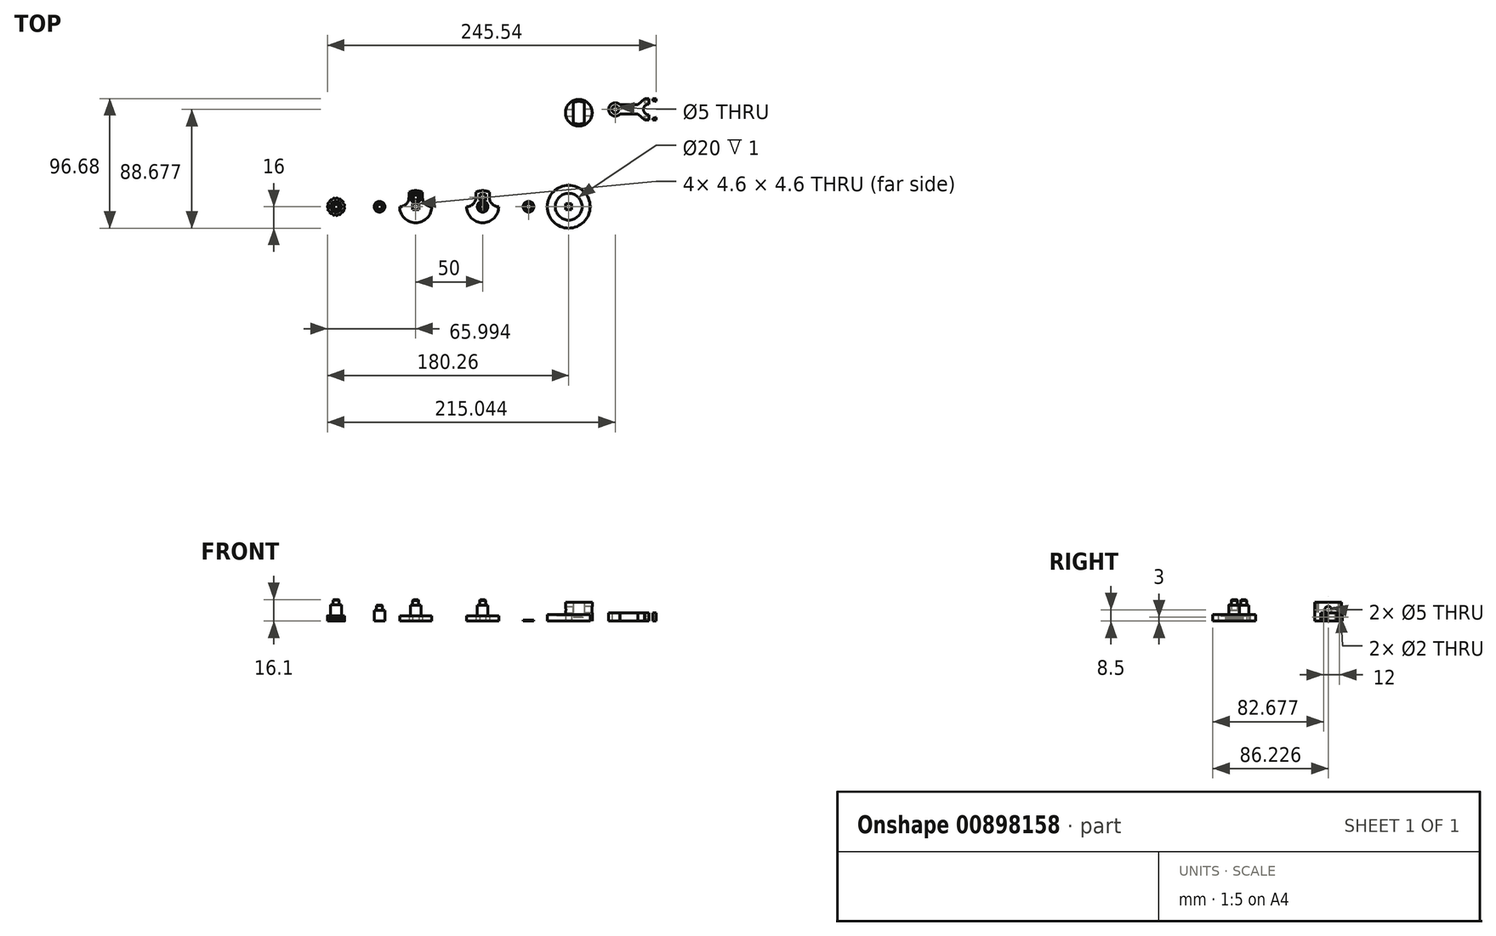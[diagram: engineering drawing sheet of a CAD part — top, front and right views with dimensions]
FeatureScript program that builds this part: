
annotation { "Feature Type Name" : "Feature", "Feature Type Description" : "" }
export const myFeature = defineFeature(function(context is Context, id is Id, definition is map)
    precondition{}
    {
        {
            var Q0;
            Q0=qCreatedBy(makeId("Top.planeOp"),FACE);
            var sketch = newSketch(context, id + "F0", { "sketchPlane" : qUnion([Q0])});
            skLineSegment(sketch, "E0", {"start": v(0, 27.68) * mm, "end": v(0, 49.61) * mm});
            skCircle(sketch, "E1", {"center": v(14.78, 62.68) * mm, "radius": 2.5 * mm});
            skPoint(sketch, "E2", {"position": v(39.78, 62.68) * mm});
            skArc(sketch, "E3", {"start": v(39.78, 58.68) * mm, "mid": v(35.78, 62.68) * mm, "end": v(39.78, 66.68) * mm});
            skLineSegment(sketch, "E4", {"start": v(39.78, 66.68) * mm, "end": v(39.78, 70.68) * mm});
            skLineSegment(sketch, "E5", {"start": v(39.78, 58.68) * mm, "end": v(39.78, 54.68) * mm});
            skPoint(sketch, "E6", {"position": v(42.78, 62.68) * mm});
            skArc(sketch, "E7", {"start": v(42.78, 66.68) * mm, "mid": v(46.78, 62.68) * mm, "end": v(42.78, 58.68) * mm});
            skArc(sketch, "E8", {"start": v(42.78, 69.18) * mm, "mid": v(49.28, 62.68) * mm, "end": v(42.78, 56.18) * mm});
            skLineSegment(sketch, "E9", {"start": v(42.78, 66.68) * mm, "end": v(42.78, 69.18) * mm});
            skLineSegment(sketch, "E10", {"start": v(42.78, 69.18) * mm, "end": v(42.78, 70.68) * mm});
            skLineSegment(sketch, "E11", {"start": v(42.78, 70.68) * mm, "end": v(45.28, 70.68) * mm});
            skLineSegment(sketch, "E12", {"start": v(45.28, 70.68) * mm, "end": v(45.28, 68.68) * mm});
            skLineSegment(sketch, "E13", {"start": v(42.78, 58.68) * mm, "end": v(42.78, 56.18) * mm});
            skLineSegment(sketch, "E14", {"start": v(42.78, 56.18) * mm, "end": v(42.78, 54.68) * mm});
            skLineSegment(sketch, "E15", {"start": v(42.78, 54.68) * mm, "end": v(45.28, 54.68) * mm});
            skLineSegment(sketch, "E16", {"start": v(45.28, 54.68) * mm, "end": v(45.28, 56.68) * mm});
            skCircle(sketch, "E17", {"center": v(-12.45, 60.23) * mm, "radius": 10 * mm});
            skLineSegment(sketch, "E18", {"start": v(18.36, 66.18) * mm, "end": v(31.78, 66.18) * mm});
            skLineSegment(sketch, "E19", {"start": v(39.78, 70.68) * mm, "end": v(36.78, 70.68) * mm});
            skLineSegment(sketch, "E20", {"start": v(36.78, 70.68) * mm, "end": v(31.78, 66.18) * mm});
            skLineSegment(sketch, "E21", {"start": v(39.78, 62.68) * mm, "end": v(42.78, 62.68) * mm});
            skLineSegment(sketch, "E22.MirrorCS", {"start": v(18.36, 59.18) * mm, "end": v(31.78, 59.18) * mm});
            skLineSegment(sketch, "E23.MirrorCS", {"start": v(39.78, 54.68) * mm, "end": v(36.78, 54.68) * mm});
            skLineSegment(sketch, "E24.MirrorCS", {"start": v(36.78, 54.68) * mm, "end": v(31.78, 59.18) * mm});
            skArc(sketch, "E25", {"start": v(18.36, 66.18) * mm, "mid": v(9.78, 62.68) * mm, "end": v(18.36, 59.18) * mm});
            skCircle(sketch, "E26", {"center": v(-134.27, -10) * mm, "radius": 12 * mm});
            skCircle(sketch, "E27", {"center": v(-134.27, -3) * mm, "radius": 4 * mm});
            skLineSegment(sketch, "E28.bottom", {"start": v(-131.97, -7.7) * mm, "end": v(-136.57, -7.7) * mm});
            skLineSegment(sketch, "E28.top", {"start": v(-131.97, -12.3) * mm, "end": v(-136.57, -12.3) * mm});
            skLineSegment(sketch, "E28.left", {"start": v(-131.97, -7.7) * mm, "end": v(-131.97, -12.3) * mm});
            skLineSegment(sketch, "E28.right", {"start": v(-136.57, -7.7) * mm, "end": v(-136.57, -12.3) * mm});
            skLineSegment(sketch, "E29.bottom", {"start": v(-132.02, -0.75) * mm, "end": v(-136.52, -0.75) * mm});
            skLineSegment(sketch, "E29.top", {"start": v(-132.02, -5.25) * mm, "end": v(-136.52, -5.25) * mm});
            skLineSegment(sketch, "E29.left", {"start": v(-132.02, -0.75) * mm, "end": v(-132.02, -5.25) * mm});
            skLineSegment(sketch, "E29.right", {"start": v(-136.52, -0.75) * mm, "end": v(-136.52, -5.25) * mm});
            skCircle(sketch, "E30", {"center": v(-84.27, -10) * mm, "radius": 12 * mm});
            skPoint(sketch, "E30.centerSnap0", {"position": v(-131.97, -10) * mm});
            skPoint(sketch, "E31", {"position": v(-84.27, -3) * mm});
            skPoint(sketch, "E31.positionSnap0", {"position": v(-132.02, -3) * mm});
            skLineSegment(sketch, "E32.bottom", {"start": v(-81.97, -0.7) * mm, "end": v(-86.57, -0.7) * mm});
            skLineSegment(sketch, "E32.top", {"start": v(-81.97, -5.3) * mm, "end": v(-86.57, -5.3) * mm});
            skLineSegment(sketch, "E32.left", {"start": v(-81.97, -0.7) * mm, "end": v(-81.97, -5.3) * mm});
            skLineSegment(sketch, "E32.right", {"start": v(-86.57, -0.7) * mm, "end": v(-86.57, -5.3) * mm});
            skCircle(sketch, "E33", {"center": v(-84.27, -10) * mm, "radius": 4 * mm});
            skCircle(sketch, "E34", {"center": v(-161.27, -10) * mm, "radius": 4 * mm});
            skLineSegment(sketch, "E35.bottom", {"start": v(-159.02, -7.75) * mm, "end": v(-163.52, -7.75) * mm});
            skLineSegment(sketch, "E35.top", {"start": v(-159.02, -12.25) * mm, "end": v(-163.52, -12.25) * mm});
            skLineSegment(sketch, "E35.left", {"start": v(-159.02, -7.75) * mm, "end": v(-159.02, -12.25) * mm});
            skLineSegment(sketch, "E35.right", {"start": v(-163.52, -7.75) * mm, "end": v(-163.52, -12.25) * mm});
            skLineSegment(sketch, "E36", {"start": v(-122.27, -10) * mm, "end": v(-122.27, -3.2) * mm});
            skPoint(sketch, "E37.startSnap0", {"position": v(-134.27, -5.25) * mm});
            skPoint(sketch, "E38", {"position": v(-122.27, -3) * mm});
            skArc(sketch, "E39", {"start": v(-122.27, -10) * mm, "mid": v(-127.22, -7.95) * mm, "end": v(-129.27, -3) * mm});
            skLineSegment(sketch, "E40", {"start": v(-129.27, -3) * mm, "end": v(-129.27, 0.9) * mm});
            skLineSegment(sketch, "E41", {"start": v(-134.27, -33.2) * mm, "end": v(-134.27, -38.63) * mm});
            skPoint(sketch, "E41.startSnap0", {"position": v(-134.27, -12.3) * mm});
            skArc(sketch, "E42.MirrorCS", {"start": v(-146.27, -10) * mm, "mid": v(-141.32, -7.95) * mm, "end": v(-139.27, -3) * mm});
            skLineSegment(sketch, "E43.MirrorCS", {"start": v(-139.27, -3) * mm, "end": v(-139.27, 0.9) * mm});
            skLineSegment(sketch, "E44.1.0.0", {"start": v(-79.27, -3) * mm, "end": v(-79.27, 0.9) * mm});
            skArc(sketch, "E44.1.0.1", {"start": v(-72.27, -10) * mm, "mid": v(-77.22, -7.95) * mm, "end": v(-79.27, -3) * mm});
            skArc(sketch, "E44.1.0.2", {"start": v(-96.27, -10) * mm, "mid": v(-91.32, -7.95) * mm, "end": v(-89.27, -3) * mm});
            skLineSegment(sketch, "E44.1.0.3", {"start": v(-89.27, -3) * mm, "end": v(-89.27, 0.9) * mm});
            skLineSegment(sketch, "E44.direction1", {"start": v(-146.27, -10) * mm, "end": v(-96.27, -10) * mm, "construction": true});
            skLineSegment(sketch, "E45.bottom", {"start": v(-82.02, -7.75) * mm, "end": v(-86.52, -7.75) * mm});
            skLineSegment(sketch, "E45.top", {"start": v(-82.02, -12.25) * mm, "end": v(-86.52, -12.25) * mm});
            skLineSegment(sketch, "E45.left", {"start": v(-82.02, -7.75) * mm, "end": v(-82.02, -12.25) * mm});
            skLineSegment(sketch, "E45.right", {"start": v(-86.52, -7.75) * mm, "end": v(-86.52, -12.25) * mm});
            skCircle(sketch, "E46", {"center": v(-20, -10) * mm, "radius": 16 * mm});
            skLineSegment(sketch, "E47.bottom", {"start": v(-17.7, -7.7) * mm, "end": v(-22.3, -7.7) * mm});
            skLineSegment(sketch, "E47.top", {"start": v(-17.7, -12.3) * mm, "end": v(-22.3, -12.3) * mm});
            skLineSegment(sketch, "E47.left", {"start": v(-17.7, -7.7) * mm, "end": v(-17.7, -12.3) * mm});
            skLineSegment(sketch, "E47.right", {"start": v(-22.3, -7.7) * mm, "end": v(-22.3, -12.3) * mm});
            skCircle(sketch, "E48", {"center": v(-50, -10) * mm, "radius": 4 * mm});
            skLineSegment(sketch, "E49.bottom", {"start": v(-47.7, -7.7) * mm, "end": v(-52.3, -7.7) * mm});
            skLineSegment(sketch, "E49.top", {"start": v(-47.7, -12.3) * mm, "end": v(-52.3, -12.3) * mm});
            skLineSegment(sketch, "E49.left", {"start": v(-47.7, -7.7) * mm, "end": v(-47.7, -12.3) * mm});
            skLineSegment(sketch, "E49.right", {"start": v(-52.3, -7.7) * mm, "end": v(-52.3, -12.3) * mm});
            skCircle(sketch, "E50", {"center": v(-193.76, -10) * mm, "radius": 4 * mm});
            skCircle(sketch, "E51", {"center": v(-193.76, -10) * mm, "radius": 6 * mm});
            skLineSegment(sketch, "E52.bottom", {"start": v(-191.51, -7.75) * mm, "end": v(-196.01, -7.75) * mm});
            skLineSegment(sketch, "E52.top", {"start": v(-191.51, -12.25) * mm, "end": v(-196.01, -12.25) * mm});
            skLineSegment(sketch, "E52.left", {"start": v(-191.51, -7.75) * mm, "end": v(-191.51, -12.25) * mm});
            skLineSegment(sketch, "E52.right", {"start": v(-196.01, -7.75) * mm, "end": v(-196.01, -12.25) * mm});
            skCircle(sketch, "E53", {"center": v(-193.76, -10) * mm, "radius": 6.5 * mm});
            skLineSegment(sketch, "E54", {"start": v(-193.76, -4) * mm, "end": v(-193.76, -3.5) * mm});
            skLineSegment(sketch, "E55.1.0", {"start": v(-195.01, -4.13) * mm, "end": v(-195.11, -3.64) * mm});
            skLineSegment(sketch, "E55.2.0", {"start": v(-196.2, -4.52) * mm, "end": v(-196.4, -4.06) * mm});
            skLineSegment(sketch, "E55.3.0", {"start": v(-197.29, -5.15) * mm, "end": v(-197.58, -4.74) * mm});
            skLineSegment(sketch, "E55.4.0", {"start": v(-198.22, -5.99) * mm, "end": v(-198.6, -5.65) * mm});
            skLineSegment(sketch, "E55.5.0", {"start": v(-198.96, -7) * mm, "end": v(-199.4, -6.75) * mm});
            skLineSegment(sketch, "E55.6.0", {"start": v(-199.47, -8.15) * mm, "end": v(-199.94, -8) * mm});
            skLineSegment(sketch, "E55.7.0", {"start": v(-199.73, -9.37) * mm, "end": v(-200.23, -9.32) * mm});
            skLineSegment(sketch, "E55.8.0", {"start": v(-199.73, -10.63) * mm, "end": v(-200.23, -10.68) * mm});
            skLineSegment(sketch, "E55.9.0", {"start": v(-199.47, -11.85) * mm, "end": v(-199.94, -12) * mm});
            skLineSegment(sketch, "E55.10.0", {"start": v(-198.96, -13) * mm, "end": v(-199.4, -13.25) * mm});
            skLineSegment(sketch, "E55.11.0", {"start": v(-198.22, -14.01) * mm, "end": v(-198.6, -14.35) * mm});
            skLineSegment(sketch, "E55.12.0", {"start": v(-197.29, -14.85) * mm, "end": v(-197.58, -15.26) * mm});
            skLineSegment(sketch, "E55.13.0", {"start": v(-196.2, -15.48) * mm, "end": v(-196.4, -15.94) * mm});
            skLineSegment(sketch, "E55.14.0", {"start": v(-195.01, -15.87) * mm, "end": v(-195.11, -16.36) * mm});
            skLineSegment(sketch, "E55.15.0", {"start": v(-193.76, -16) * mm, "end": v(-193.76, -16.5) * mm});
            skLineSegment(sketch, "E55.16.0", {"start": v(-192.52, -15.87) * mm, "end": v(-192.41, -16.36) * mm});
            skLineSegment(sketch, "E55.17.0", {"start": v(-191.32, -15.48) * mm, "end": v(-191.12, -15.94) * mm});
            skLineSegment(sketch, "E55.18.0", {"start": v(-190.24, -14.85) * mm, "end": v(-189.94, -15.26) * mm});
            skLineSegment(sketch, "E55.19.0", {"start": v(-189.3, -14.01) * mm, "end": v(-188.93, -14.35) * mm});
            skLineSegment(sketch, "E55.20.0", {"start": v(-188.57, -13) * mm, "end": v(-188.13, -13.25) * mm});
            skLineSegment(sketch, "E55.21.0", {"start": v(-188.06, -11.85) * mm, "end": v(-187.58, -12) * mm});
            skLineSegment(sketch, "E55.22.0", {"start": v(-187.8, -10.63) * mm, "end": v(-187.3, -10.68) * mm});
            skLineSegment(sketch, "E55.23.0", {"start": v(-187.8, -9.37) * mm, "end": v(-187.3, -9.32) * mm});
            skLineSegment(sketch, "E55.24.0", {"start": v(-188.06, -8.15) * mm, "end": v(-187.58, -8) * mm});
            skLineSegment(sketch, "E55.25.0", {"start": v(-188.57, -7) * mm, "end": v(-188.13, -6.75) * mm});
            skLineSegment(sketch, "E55.26.0", {"start": v(-189.3, -5.99) * mm, "end": v(-188.93, -5.65) * mm});
            skLineSegment(sketch, "E55.27.0", {"start": v(-190.24, -5.15) * mm, "end": v(-189.94, -4.74) * mm});
            skLineSegment(sketch, "E55.28.0", {"start": v(-191.32, -4.52) * mm, "end": v(-191.12, -4.06) * mm});
            skLineSegment(sketch, "E55.29.0", {"start": v(-192.52, -4.13) * mm, "end": v(-192.41, -3.64) * mm});
            skSolve(sketch);
        }
        {
            var Q0;
            Q0=makeQuery(id+"F0.imprint","IMPRINT",FACE,{"disambiguationData":[TD([[makeQuery(id+"F0.imprint","IMPRINT",EDGE,{"derivedFrom":sQuery(id+"F0.wireOp",EDGE,"E1")}),-1.0]])]});
            var Q1;
            Q1=makeQuery(id+"F0.imprint","IMPRINT",FACE,{"disambiguationData":[TD([[makeQuery(id+"F0.imprint","IMPRINT",EDGE,{"derivedFrom":sQuery(id+"F0.wireOp",EDGE,"E7")}),1.0]])]});
            var Q2;
            {var subQ0=sQuery(id+"F0.wireOp",EDGE,"E10");Q2=makeQuery(id+"F0.imprint","IMPRINT",FACE,{"disambiguationData":[TD([[makeQuery(id+"F0.imprint","IMPRINT",EDGE,{"derivedFrom":subQ0}),-1.0]])]});}
            var Q3;
            {var subQ0=sQuery(id+"F0.wireOp",EDGE,"E14");Q3=makeQuery(id+"F0.imprint","IMPRINT",FACE,{"disambiguationData":[TD([[makeQuery(id+"F0.imprint","IMPRINT",EDGE,{"derivedFrom":subQ0}),1.0]])]});}
            extrude(context, id + "F1", {"entities" : qUnion([Q0, Q1, Q2, Q3]), "depth" : 6 * mm, "offsetDistance" : 25 * mm});
        }
        {
            var Q0;
            Q0=makeQuery(id+"F1.opExtrude","SWEPT_FACE",FACE,{"disambiguationData":[OSD([sQuery(id+"F0.wireOp",EDGE,"E9"),sQuery(id+"F0.wireOp",EDGE,"E10")])]});
            var sketch = newSketch(context, id + "F2", { "sketchPlane" : qUnion([Q0])});
            skPoint(sketch, "E56", {"position": v(-68.68, 3) * mm});
            skPoint(sketch, "E57", {"position": v(-56.68, 3) * mm});
            skSolve(sketch);
        }
        {
            var Q0;
            Q0=sQuery(id+"F2.wireOp",VERTEX,"E56");
            var Q1;
            Q1=sQuery(id+"F2.wireOp",VERTEX,"E57");
            var Q2;
            Q2=makeQuery(id+"F1.opExtrude","SWEPT_BODY",BODY,{"disambiguationData":[OSD([sQuery(id+"F0.wireOp",EDGE,"E7"),sQuery(id+"F0.wireOp",EDGE,"E8"),sQuery(id+"F0.wireOp",EDGE,"E9"),sQuery(id+"F0.wireOp",EDGE,"E10"),sQuery(id+"F0.wireOp",EDGE,"E11"),sQuery(id+"F0.wireOp",EDGE,"E12"),sQuery(id+"F0.wireOp",EDGE,"E13"),sQuery(id+"F0.wireOp",EDGE,"E14"),sQuery(id+"F0.wireOp",EDGE,"E15"),sQuery(id+"F0.wireOp",EDGE,"E16")])]});
            hole(context, id + "F3", {"style" : HoleStyle.SIMPLE, "endStyle" : HoleEndStyle.THROUGH, "holeDiameter" : 2.2 * mm, "majorDiameter" : 5 * mm, "isTappedThrough" : true, "tappedDepth" : 12 * mm, "tapClearance" : 3, "locations" : qUnion([Q0, Q1]), "scope" : qUnion([Q2])});
        }
        {
            var Q0;
            Q0=makeQuery(id+"F1.opExtrude","SWEPT_FACE",FACE,{"disambiguationData":[OSD([sQuery(id+"F0.wireOp",EDGE,"E12")])]});
            var sketch = newSketch(context, id + "F4", { "sketchPlane" : qUnion([Q0])});
            skPoint(sketch, "E58", {"position": v(68.7, 2.96) * mm});
            skPoint(sketch, "E59", {"position": v(56.68, 2.96) * mm});
            skCircle(sketch, "E60", {"center": v(56.68, 2.96) * mm, "radius": 2.1 * mm});
            skCircle(sketch, "E61", {"center": v(68.7, 2.96) * mm, "radius": 2.1 * mm});
            skSolve(sketch);
        }
        {
            var Q0;
            Q0=makeQuery(id+"F4.imprint","IMPRINT",FACE,{"disambiguationData":[TD([[makeQuery(id+"F4.imprint","IMPRINT",EDGE,{"derivedFrom":sQuery(id+"F4.wireOp",EDGE,"E60")}),1.0]])]});
            var Q1;
            {var subQ5=sQuery(id+"F0.wireOp",EDGE,"E12");var subQ12=makeQuery(id+"F1.opExtrude","SWEPT_FACE",FACE,{"disambiguationData":[OSD([subQ5])]});var subQ13=makeQuery(id+"F3.hole-0.opRevolve","SWEPT_FACE",FACE,{"disambiguationData":[OSD([sQuery(id+"F3.hole-0.sketch.wireOp",EDGE,"core_line_2")])]});var subQ19=makeQuery(id+"F3.hole-0.boolean.opBoolean","INTERSECT",EDGE,{"derivedFrom":[subQ12,subQ13]});Q1=makeQuery(id+"F4.imprint","IMPRINT",FACE,{"disambiguationData":[TD([[makeQuery(id+"F4.imprint","IMPRINT",EDGE,{"derivedFrom":subQ19}),-1.0]])]});}
            extrude(context, id + "F5", {"entities" : qUnion([Q0, Q1]), "operationType" : NewBodyOperationType.REMOVE, "depth" : 25 * mm, "offsetDistance" : 25 * mm});
        }
        {
            var Q0;
            Q0=makeQuery(id+"F0.imprint","IMPRINT",FACE,{"disambiguationData":[TD([[makeQuery(id+"F0.imprint","IMPRINT",EDGE,{"derivedFrom":sQuery(id+"F0.wireOp",EDGE,"E17")}),1.0]])]});
            extrude(context, id + "F6", {"entities" : qUnion([Q0]), "depth" : 3 * mm, "offsetDistance" : 25 * mm});
        }
        {
            var Q0;
            Q0=makeQuery(id+"F6.opExtrude","CAP_FACE",FACE,{"disambiguationData":[OSD([sQuery(id+"F0.wireOp",EDGE,"E17")])],"isStart":false});
            var sketch = newSketch(context, id + "F7", { "sketchPlane" : qUnion([Q0])});
            skCircle(sketch, "E62", {"center": v(-12.45, 60.23) * mm, "radius": 8.5 * mm});
            skLineSegment(sketch, "E63", {"start": v(-16.45, 67.73) * mm, "end": v(-16.45, 52.73) * mm});
            skLineSegment(sketch, "E64", {"start": v(-8.45, 67.73) * mm, "end": v(-8.45, 52.73) * mm});
            skSolve(sketch);
        }
        {
            var Q0;
            Q0=makeQuery(id+"F7.imprint","IMPRINT",FACE,{"disambiguationData":[TD([[makeQuery(id+"F7.imprint","IMPRINT",EDGE,{"derivedFrom":makeQuery(id+"F6.opExtrude","CAP_EDGE",EDGE,{"disambiguationData":[OSD([sQuery(id+"F0.wireOp",EDGE,"E17")])],"isStart":false})}),1.0]])]});
            var Q1;
            {var subQ0=sQuery(id+"F7.wireOp",EDGE,"E63");Q1=makeQuery(id+"F7.imprint","IMPRINT",FACE,{"disambiguationData":[TD([[makeQuery(id+"F7.imprint","IMPRINT",EDGE,{"derivedFrom":subQ0}),-1.0]])]});}
            var Q2;
            {var subQ0=sQuery(id+"F7.wireOp",EDGE,"E64");Q2=makeQuery(id+"F7.imprint","IMPRINT",FACE,{"disambiguationData":[TD([[makeQuery(id+"F7.imprint","IMPRINT",EDGE,{"derivedFrom":subQ0}),1.0]])]});}
            extrude(context, id + "F8", {"entities" : qUnion([Q0, Q1, Q2]), "operationType" : NewBodyOperationType.ADD, "depth" : 11 * mm, "offsetDistance" : 25 * mm});
        }
        {
            var Q0;
            Q0=makeQuery(id+"F1.opExtrude","SWEPT_FACE",FACE,{"disambiguationData":[OSD([sQuery(id+"F0.wireOp",EDGE,"E4")])]});
            var sketch = newSketch(context, id + "F9", { "sketchPlane" : qUnion([Q0])});
            skPoint(sketch, "E65", {"position": v(56.68, 3) * mm});
            skPoint(sketch, "E66", {"position": v(68.68, 3) * mm});
            skSolve(sketch);
        }
        {
            var Q0;
            Q0=sQuery(id+"F9.wireOp",VERTEX,"E65");
            var Q1;
            Q1=sQuery(id+"F9.wireOp",VERTEX,"E66");
            var Q2;
            Q2=makeQuery(id+"F1.opExtrude","SWEPT_BODY",BODY,{"disambiguationData":[OSD([sQuery(id+"F0.wireOp",EDGE,"E1"),sQuery(id+"F0.wireOp",EDGE,"E3"),sQuery(id+"F0.wireOp",EDGE,"E4"),sQuery(id+"F0.wireOp",EDGE,"E5"),sQuery(id+"F0.wireOp",EDGE,"E18"),sQuery(id+"F0.wireOp",EDGE,"E19"),sQuery(id+"F0.wireOp",EDGE,"E20"),sQuery(id+"F0.wireOp",EDGE,"E22.MirrorCS"),sQuery(id+"F0.wireOp",EDGE,"E23.MirrorCS"),sQuery(id+"F0.wireOp",EDGE,"E24.MirrorCS"),sQuery(id+"F0.wireOp",EDGE,"E25")])]});
            hole(context, id + "F10", {"style" : HoleStyle.SIMPLE, "endStyle" : HoleEndStyle.BLIND, "holeDiameter" : 2 * mm, "majorDiameter" : 5 * mm, "holeDepth" : 3 * mm, "isTappedThrough" : true, "tappedDepth" : 12 * mm, "tapClearance" : 3, "locations" : qUnion([Q0, Q1]), "scope" : qUnion([Q2])});
        }
        {
            var Q0;
            Q0=makeQuery(id+"F0.imprint","IMPRINT",FACE,{"disambiguationData":[TD([[makeQuery(id+"F0.imprint","IMPRINT",EDGE,{"derivedFrom":sQuery(id+"F0.wireOp",EDGE,"E27")}),1.0]])]});
            extrude(context, id + "F11", {"entities" : qUnion([Q0]), "depth" : 12 * mm, "offsetDistance" : 25 * mm});
        }
        {
            var Q0;
            Q0=makeQuery(id+"F0.imprint","IMPRINT",FACE,{"disambiguationData":[TD([[makeQuery(id+"F0.imprint","IMPRINT",EDGE,{"derivedFrom":sQuery(id+"F0.wireOp",EDGE,"E26")}),1.0]])]});
            extrude(context, id + "F12", {"entities" : qUnion([Q0]), "operationType" : NewBodyOperationType.ADD, "depth" : 4 * mm, "offsetDistance" : 25 * mm});
        }
        {
            var Q0;
            Q0=makeQuery(id+"F0.imprint","IMPRINT",FACE,{"disambiguationData":[TD([[makeQuery(id+"F0.imprint","IMPRINT",EDGE,{"derivedFrom":sQuery(id+"F0.wireOp",EDGE,"E29.bottom")}),1.0]])]});
            extrude(context, id + "F13", {"entities" : qUnion([Q0]), "operationType" : NewBodyOperationType.ADD, "depth" : 15.9 * mm, "offsetDistance" : 25 * mm});
        }
        {
            var Q0;
            Q0=makeQuery(id+"F0.imprint","IMPRINT",FACE,{"disambiguationData":[TD([[makeQuery(id+"F0.imprint","IMPRINT",EDGE,{"derivedFrom":sQuery(id+"F0.wireOp",EDGE,"E33")}),1.0]])]});
            extrude(context, id + "F14", {"entities" : qUnion([Q0]), "depth" : 12 * mm, "offsetDistance" : 25 * mm});
        }
        {
            var Q0;
            Q0=makeQuery(id+"F0.imprint","IMPRINT",FACE,{"disambiguationData":[TD([[makeQuery(id+"F0.imprint","IMPRINT",EDGE,{"derivedFrom":sQuery(id+"F0.wireOp",EDGE,"E30")}),1.0]])]});
            extrude(context, id + "F15", {"entities" : qUnion([Q0]), "operationType" : NewBodyOperationType.ADD, "depth" : 4 * mm, "offsetDistance" : 25 * mm});
        }
        {
            var Q0;
            Q0=makeQuery(id+"F0.imprint","IMPRINT",FACE,{"disambiguationData":[TD([[makeQuery(id+"F0.imprint","IMPRINT",EDGE,{"derivedFrom":sQuery(id+"F0.wireOp",EDGE,"E35.bottom")}),1.0]])]});
            extrude(context, id + "F16", {"entities" : qUnion([Q0]), "depth" : 11.9 * mm, "offsetDistance" : 25 * mm});
        }
        {
            var Q0;
            Q0=makeQuery(id+"F0.imprint","IMPRINT",FACE,{"disambiguationData":[TD([[makeQuery(id+"F0.imprint","IMPRINT",EDGE,{"derivedFrom":sQuery(id+"F0.wireOp",EDGE,"E34")}),1.0]])]});
            extrude(context, id + "F17", {"entities" : qUnion([Q0]), "operationType" : NewBodyOperationType.ADD, "depth" : 8 * mm, "offsetDistance" : 25 * mm});
        }
        {
            var Q0;
            Q0=makeQuery(id+"F0.imprint","IMPRINT",FACE,{"disambiguationData":[TD([[makeQuery(id+"F0.imprint","IMPRINT",EDGE,{"derivedFrom":sQuery(id+"F0.wireOp",EDGE,"E45.bottom")}),1.0]])]});
            extrude(context, id + "F18", {"entities" : qUnion([Q0]), "operationType" : NewBodyOperationType.ADD, "depth" : 15.9 * mm, "offsetDistance" : 25 * mm});
        }
        {
            var Q0;
            Q0=makeQuery(id+"F0.imprint","IMPRINT",FACE,{"disambiguationData":[TD([[makeQuery(id+"F0.imprint","IMPRINT",EDGE,{"derivedFrom":sQuery(id+"F0.wireOp",EDGE,"E46")}),1.0]])]});
            extrude(context, id + "F19", {"entities" : qUnion([Q0]), "depth" : 4 * mm, "offsetDistance" : 25 * mm});
        }
        {
            var Q0;
            Q0=makeQuery(id+"F19.opExtrude","CAP_FACE",FACE,{"disambiguationData":[OSD([sQuery(id+"F0.wireOp",EDGE,"E46"),sQuery(id+"F0.wireOp",EDGE,"E47.bottom"),sQuery(id+"F0.wireOp",EDGE,"E47.top"),sQuery(id+"F0.wireOp",EDGE,"E47.left"),sQuery(id+"F0.wireOp",EDGE,"E47.right")])],"isStart":false});
            var sketch = newSketch(context, id + "F20", { "sketchPlane" : qUnion([Q0])});
            skCircle(sketch, "E67", {"center": v(-20, -10) * mm, "radius": 10 * mm});
            skSolve(sketch);
        }
        {
            var Q0;
            Q0=makeQuery(id+"F20.imprint","IMPRINT",FACE,{"disambiguationData":[TD([[makeQuery(id+"F20.imprint","IMPRINT",EDGE,{"derivedFrom":sQuery(id+"F20.wireOp",EDGE,"E67")}),-1.0]])]});
            extrude(context, id + "F21", {"entities" : qUnion([Q0]), "operationType" : NewBodyOperationType.ADD, "depth" : 1 * mm, "offsetDistance" : 25 * mm});
        }
        {
            var Q0;
            Q0=makeQuery(id+"F0.imprint","IMPRINT",FACE,{"disambiguationData":[TD([[makeQuery(id+"F0.imprint","IMPRINT",EDGE,{"derivedFrom":sQuery(id+"F0.wireOp",EDGE,"E48")}),1.0]])]});
            extrude(context, id + "F22", {"entities" : qUnion([Q0]), "depth" : .7 * mm, "offsetDistance" : 25 * mm});
        }
        {
            var Q0;
            Q0=makeQuery(id+"F0.imprint","IMPRINT",FACE,{"disambiguationData":[TD([[makeQuery(id+"F0.imprint","IMPRINT",EDGE,{"derivedFrom":sQuery(id+"F0.wireOp",EDGE,"E52.bottom")}),1.0]])]});
            extrude(context, id + "F23", {"entities" : qUnion([Q0]), "depth" : 16.1 * mm, "offsetDistance" : 25 * mm});
        }
        {
            var Q0;
            Q0=makeQuery(id+"F0.imprint","IMPRINT",FACE,{"disambiguationData":[TD([[makeQuery(id+"F0.imprint","IMPRINT",EDGE,{"derivedFrom":sQuery(id+"F0.wireOp",EDGE,"E50")}),1.0]])]});
            extrude(context, id + "F24", {"entities" : qUnion([Q0]), "operationType" : NewBodyOperationType.ADD, "depth" : 12.2 * mm, "offsetDistance" : 25 * mm});
        }
        {
            var Q0;
            Q0=makeQuery(id+"F0.imprint","IMPRINT",FACE,{"disambiguationData":[TD([[makeQuery(id+"F0.imprint","IMPRINT",EDGE,{"derivedFrom":sQuery(id+"F0.wireOp",EDGE,"E50")}),-1.0]])]});
            var Q1;
            {var subQ0=sQuery(id+"F0.wireOp",EDGE,"E54");Q1=makeQuery(id+"F0.imprint","IMPRINT",FACE,{"disambiguationData":[TD([[makeQuery(id+"F0.imprint","IMPRINT",EDGE,{"derivedFrom":subQ0}),-1.0]])]});}
            var Q2;
            {var subQ0=sQuery(id+"F0.wireOp",EDGE,"E55.27.0");Q2=makeQuery(id+"F0.imprint","IMPRINT",FACE,{"disambiguationData":[TD([[makeQuery(id+"F0.imprint","IMPRINT",EDGE,{"derivedFrom":subQ0}),1.0]])]});}
            var Q3;
            {var subQ0=sQuery(id+"F0.wireOp",EDGE,"E55.25.0");Q3=makeQuery(id+"F0.imprint","IMPRINT",FACE,{"disambiguationData":[TD([[makeQuery(id+"F0.imprint","IMPRINT",EDGE,{"derivedFrom":subQ0}),1.0]])]});}
            var Q4;
            {var subQ0=sQuery(id+"F0.wireOp",EDGE,"E55.23.0");Q4=makeQuery(id+"F0.imprint","IMPRINT",FACE,{"disambiguationData":[TD([[makeQuery(id+"F0.imprint","IMPRINT",EDGE,{"derivedFrom":subQ0}),1.0]])]});}
            var Q5;
            {var subQ0=sQuery(id+"F0.wireOp",EDGE,"E55.21.0");Q5=makeQuery(id+"F0.imprint","IMPRINT",FACE,{"disambiguationData":[TD([[makeQuery(id+"F0.imprint","IMPRINT",EDGE,{"derivedFrom":subQ0}),1.0]])]});}
            var Q6;
            {var subQ0=sQuery(id+"F0.wireOp",EDGE,"E55.19.0");Q6=makeQuery(id+"F0.imprint","IMPRINT",FACE,{"disambiguationData":[TD([[makeQuery(id+"F0.imprint","IMPRINT",EDGE,{"derivedFrom":subQ0}),1.0]])]});}
            var Q7;
            {var subQ0=sQuery(id+"F0.wireOp",EDGE,"E55.17.0");Q7=makeQuery(id+"F0.imprint","IMPRINT",FACE,{"disambiguationData":[TD([[makeQuery(id+"F0.imprint","IMPRINT",EDGE,{"derivedFrom":subQ0}),1.0]])]});}
            var Q8;
            {var subQ0=sQuery(id+"F0.wireOp",EDGE,"E55.15.0");Q8=makeQuery(id+"F0.imprint","IMPRINT",FACE,{"disambiguationData":[TD([[makeQuery(id+"F0.imprint","IMPRINT",EDGE,{"derivedFrom":subQ0}),1.0]])]});}
            var Q9;
            {var subQ0=sQuery(id+"F0.wireOp",EDGE,"E55.13.0");Q9=makeQuery(id+"F0.imprint","IMPRINT",FACE,{"disambiguationData":[TD([[makeQuery(id+"F0.imprint","IMPRINT",EDGE,{"derivedFrom":subQ0}),1.0]])]});}
            var Q10;
            {var subQ0=sQuery(id+"F0.wireOp",EDGE,"E55.11.0");Q10=makeQuery(id+"F0.imprint","IMPRINT",FACE,{"disambiguationData":[TD([[makeQuery(id+"F0.imprint","IMPRINT",EDGE,{"derivedFrom":subQ0}),1.0]])]});}
            var Q11;
            {var subQ0=sQuery(id+"F0.wireOp",EDGE,"E55.9.0");Q11=makeQuery(id+"F0.imprint","IMPRINT",FACE,{"disambiguationData":[TD([[makeQuery(id+"F0.imprint","IMPRINT",EDGE,{"derivedFrom":subQ0}),1.0]])]});}
            var Q12;
            {var subQ0=sQuery(id+"F0.wireOp",EDGE,"E55.7.0");Q12=makeQuery(id+"F0.imprint","IMPRINT",FACE,{"disambiguationData":[TD([[makeQuery(id+"F0.imprint","IMPRINT",EDGE,{"derivedFrom":subQ0}),1.0]])]});}
            var Q13;
            {var subQ0=sQuery(id+"F0.wireOp",EDGE,"E55.5.0");Q13=makeQuery(id+"F0.imprint","IMPRINT",FACE,{"disambiguationData":[TD([[makeQuery(id+"F0.imprint","IMPRINT",EDGE,{"derivedFrom":subQ0}),1.0]])]});}
            var Q14;
            {var subQ0=sQuery(id+"F0.wireOp",EDGE,"E55.3.0");Q14=makeQuery(id+"F0.imprint","IMPRINT",FACE,{"disambiguationData":[TD([[makeQuery(id+"F0.imprint","IMPRINT",EDGE,{"derivedFrom":subQ0}),1.0]])]});}
            var Q15;
            {var subQ0=sQuery(id+"F0.wireOp",EDGE,"E55.1.0");Q15=makeQuery(id+"F0.imprint","IMPRINT",FACE,{"disambiguationData":[TD([[makeQuery(id+"F0.imprint","IMPRINT",EDGE,{"derivedFrom":subQ0}),1.0]])]});}
            extrude(context, id + "F25", {"entities" : qUnion([Q0, Q1, Q2, Q3, Q4, Q5, Q6, Q7, Q8, Q9, Q10, Q11, Q12, Q13, Q14, Q15]), "operationType" : NewBodyOperationType.ADD, "depth" : 4 * mm, "offsetDistance" : 25 * mm});
        }
        {
            var Q0;
            Q0=makeQuery(id+"F23.opExtrude","CAP_EDGE",EDGE,{"disambiguationData":[OSD([sQuery(id+"F0.wireOp",EDGE,"E52.right")])],"isStart":false});
            var Q1;
            Q1=makeQuery(id+"F23.opExtrude","CAP_EDGE",EDGE,{"disambiguationData":[OSD([sQuery(id+"F0.wireOp",EDGE,"E52.bottom")])],"isStart":false});
            var Q2;
            Q2=makeQuery(id+"F23.opExtrude","CAP_EDGE",EDGE,{"disambiguationData":[OSD([sQuery(id+"F0.wireOp",EDGE,"E52.left")])],"isStart":false});
            var Q3;
            Q3=makeQuery(id+"F23.opExtrude","CAP_EDGE",EDGE,{"disambiguationData":[OSD([sQuery(id+"F0.wireOp",EDGE,"E52.top")])],"isStart":false});
            var Q4;
            Q4=makeQuery(id+"F16.opExtrude","CAP_FACE",FACE,{"disambiguationData":[OSD([sQuery(id+"F0.wireOp",EDGE,"E35.bottom"),sQuery(id+"F0.wireOp",EDGE,"E35.top"),sQuery(id+"F0.wireOp",EDGE,"E35.left"),sQuery(id+"F0.wireOp",EDGE,"E35.right")])],"isStart":false});
            var Q5;
            Q5=makeQuery(id+"F13.opExtrude","CAP_FACE",FACE,{"disambiguationData":[OSD([sQuery(id+"F0.wireOp",EDGE,"E29.bottom"),sQuery(id+"F0.wireOp",EDGE,"E29.top"),sQuery(id+"F0.wireOp",EDGE,"E29.left"),sQuery(id+"F0.wireOp",EDGE,"E29.right")])],"isStart":false});
            var Q6;
            Q6=makeQuery(id+"F18.opExtrude","CAP_FACE",FACE,{"disambiguationData":[OSD([sQuery(id+"F0.wireOp",EDGE,"E45.bottom"),sQuery(id+"F0.wireOp",EDGE,"E45.top"),sQuery(id+"F0.wireOp",EDGE,"E45.left"),sQuery(id+"F0.wireOp",EDGE,"E45.right")])],"isStart":false});
            chamfer(context, id + "F26", {"entities" : qUnion([Q0, Q1, Q2, Q3, Q4, Q5, Q6]), "width" : 0.5 * mm, "tangentPropagation" : true});
        }
        {
            var Q0;
            Q0=makeQuery(id+"F8.opExtrude","SWEPT_FACE",FACE,{"disambiguationData":[OSD([sQuery(id+"F7.wireOp",EDGE,"E64")])]});
            var sketch = newSketch(context, id + "F27", { "sketchPlane" : qUnion([Q0])});
            skPoint(sketch, "E68", {"position": v(-60.23, 8.5) * mm});
            skPoint(sketch, "E68.positionSnap0", {"position": v(-60.23, 14) * mm});
            skSolve(sketch);
        }
        {
            var Q0;
            Q0=sQuery(id+"F27.wireOp",VERTEX,"E68");
            var Q1;
            Q1=makeQuery(id+"F6.opExtrude","SWEPT_BODY",BODY,{"disambiguationData":[OSD([sQuery(id+"F0.wireOp",EDGE,"E17")])]});
            hole(context, id + "F28", {"style" : HoleStyle.SIMPLE, "endStyle" : HoleEndStyle.BLIND, "oppositeDirection" : true, "holeDiameter" : 5 * mm, "majorDiameter" : 5 * mm, "holeDepth" : 15 * mm, "isTappedThrough" : true, "tappedDepth" : 12 * mm, "tapClearance" : 3, "locations" : qUnion([Q0]), "scope" : qUnion([Q1])});
        }
        {
            var Q0;
            Q0=sQuery(id+"F27.wireOp",VERTEX,"E68");
            var Q1;
            Q1=makeQuery(id+"F6.opExtrude","SWEPT_BODY",BODY,{"disambiguationData":[OSD([sQuery(id+"F0.wireOp",EDGE,"E17")])]});
            hole(context, id + "F29", {"style" : HoleStyle.SIMPLE, "endStyle" : HoleEndStyle.BLIND, "holeDiameter" : 5 * mm, "majorDiameter" : 5 * mm, "holeDepth" : 10 * mm, "isTappedThrough" : true, "tappedDepth" : 12 * mm, "tapClearance" : 3, "locations" : qUnion([Q0]), "scope" : qUnion([Q1])});
        }
    });
